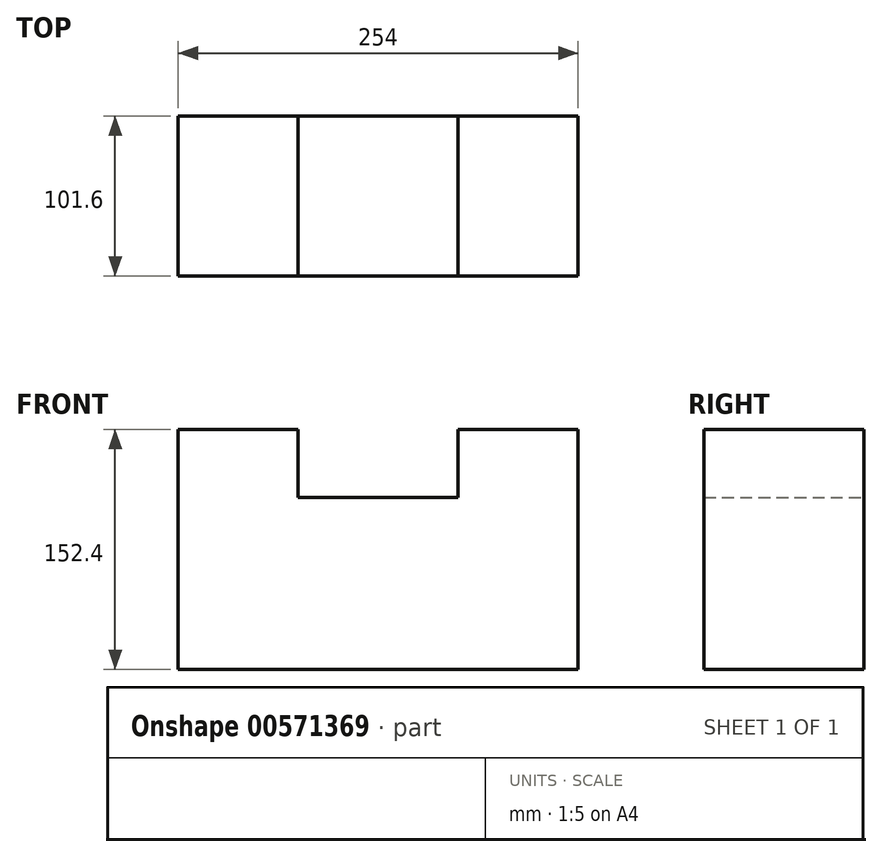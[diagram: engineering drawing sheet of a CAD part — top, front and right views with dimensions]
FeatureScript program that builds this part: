
annotation { "Feature Type Name" : "Feature", "Feature Type Description" : "" }
export const myFeature = defineFeature(function(context is Context, id is Id, definition is map)
    precondition{}
    {
        {
            var Q0;
            Q0=qCreatedBy(makeId("Front.planeOp"),FACE);
            var sketch = newSketch(context, id + "F0", { "sketchPlane" : qUnion([Q0])});
            skLineSegment(sketch, "E0", {"start": v(0, 0) * mm, "end": v(254, 0) * mm});
            skLineSegment(sketch, "E1", {"start": v(254, 0) * mm, "end": v(254, 152.4) * mm});
            skLineSegment(sketch, "E2", {"start": v(254, 152.4) * mm, "end": v(177.8, 152.4) * mm});
            skLineSegment(sketch, "E3", {"start": v(177.8, 152.4) * mm, "end": v(177.8, 109.1) * mm});
            skLineSegment(sketch, "E4", {"start": v(177.8, 109.1) * mm, "end": v(76.2, 109.1) * mm});
            skLineSegment(sketch, "E5", {"start": v(76.2, 109.1) * mm, "end": v(76.2, 152.4) * mm});
            skLineSegment(sketch, "E6", {"start": v(76.2, 152.4) * mm, "end": v(0, 152.4) * mm});
            skLineSegment(sketch, "E7", {"start": v(0, 152.4) * mm, "end": v(0, 0) * mm});
            skSolve(sketch);
        }
        {
            var Q0;
            Q0 = qSketchRegion(id + "F0", true);
            extrude(context, id + "F1", {"entities" : qUnion([Q0]), "depth" : 101.6 * mm, "offsetDistance" : 25.4 * mm});
        }
    });
